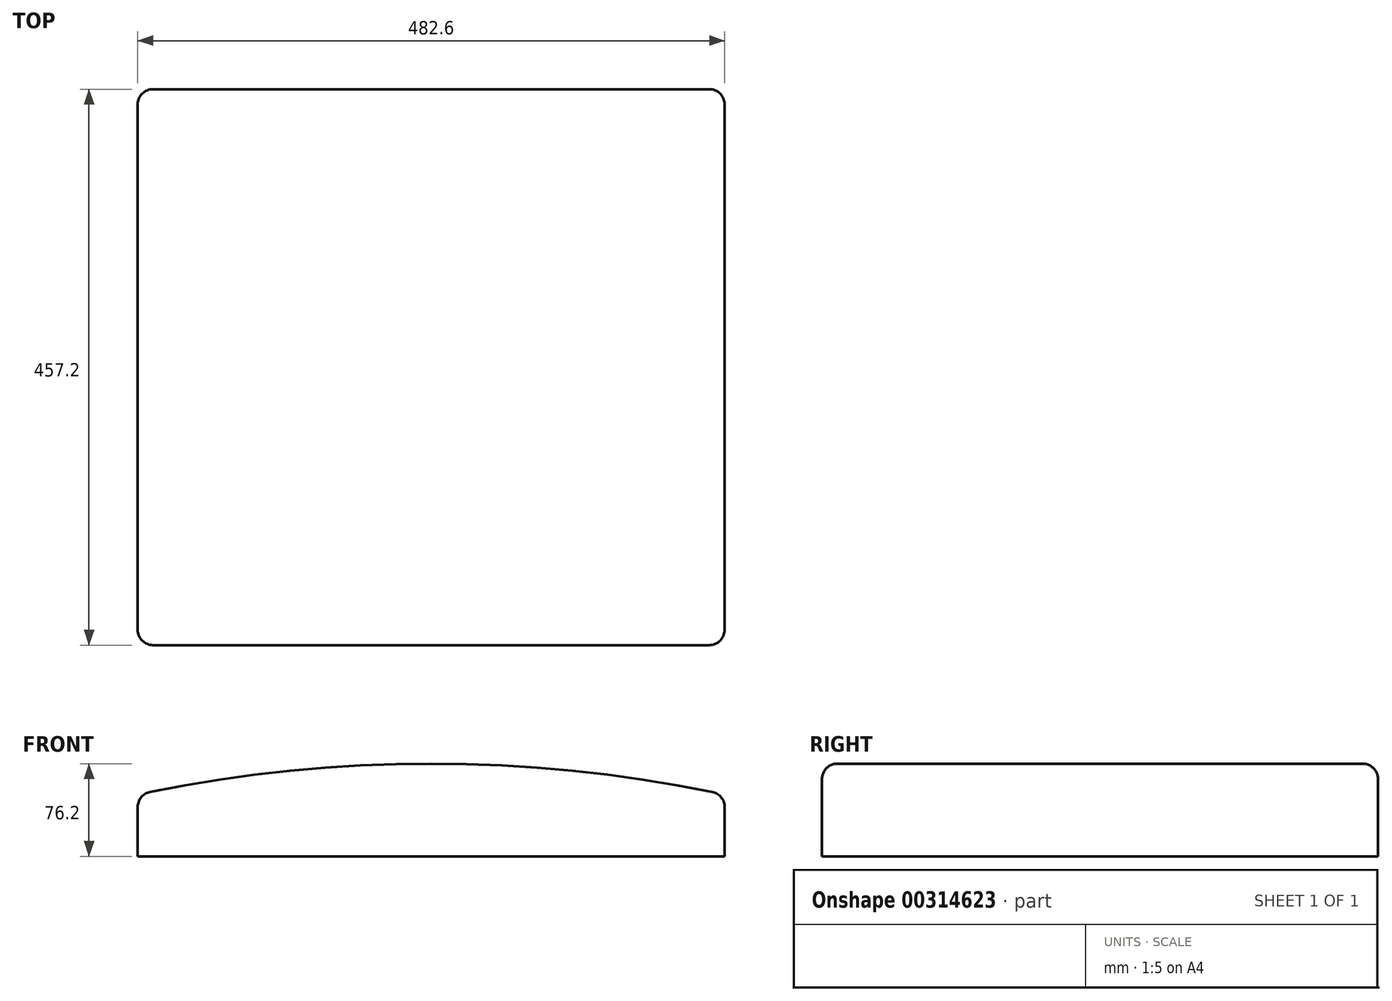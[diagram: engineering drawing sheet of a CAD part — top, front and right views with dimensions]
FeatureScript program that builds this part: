
annotation { "Feature Type Name" : "Feature", "Feature Type Description" : "" }
export const myFeature = defineFeature(function(context is Context, id is Id, definition is map)
    precondition{}
    {
        {
            var Q0;
            Q0=qCreatedBy(makeId("Front.planeOp"),FACE);
            var sketch = newSketch(context, id + "F0", { "sketchPlane" : qUnion([Q0])});
            skLineSegment(sketch, "E0.bottom", {"start": v(241.3, -25.4) * mm, "end": v(-241.3, -25.4) * mm});
            skLineSegment(sketch, "E0.top", {"start": v(241.3, 25.4) * mm, "end": v(-241.3, 25.4) * mm});
            skLineSegment(sketch, "E0.left", {"start": v(241.3, -25.4) * mm, "end": v(241.3, 25.4) * mm});
            skLineSegment(sketch, "E0.right", {"start": v(-241.3, -25.4) * mm, "end": v(-241.3, 25.4) * mm});
            skPoint(sketch, "E0.middle", {"position": v(0, 0) * mm});
            skArc(sketch, "E1", {"start": v(241.3, 25.4) * mm, "mid": v(0, 50.8) * mm, "end": v(-241.3, 25.4) * mm});
            skSolve(sketch);
        }
        {
            var Q0;
            Q0=makeQuery(id+"F0.imprint","IMPRINT",FACE,{"disambiguationData":[TD([[makeQuery(id+"F0.imprint","IMPRINT",EDGE,{"derivedFrom":sQuery(id+"F0.wireOp",EDGE,"E0.top")}),-1.0]])]});
            extrude(context, id + "F1", {"entities" : qUnion([Q0]), "endBound" : BoundingType.SYMMETRIC, "depth" : 457.2 * mm});
        }
        {
            var Q0;
            Q0 = qSketchRegion(id + "F0", true);
            extrude(context, id + "F2", {"entities" : qUnion([Q0]), "operationType" : NewBodyOperationType.ADD, "endBound" : BoundingType.SYMMETRIC, "depth" : 457.2 * mm});
        }
        {
            var Q0;
            Q0=makeQuery(id+"F2.opExtrude","CAP_EDGE",EDGE,{"disambiguationData":[OSD([sQuery(id+"F0.wireOp",EDGE,"E0.right")])],"isStart":true});
            var Q1;
            Q1=makeQuery(id+"F2.opExtrude","CAP_EDGE",EDGE,{"disambiguationData":[OSD([sQuery(id+"F0.wireOp",EDGE,"E0.right")])],"isStart":false});
            var Q2;
            Q2=makeQuery(id+"F2.opExtrude","CAP_EDGE",EDGE,{"disambiguationData":[OSD([sQuery(id+"F0.wireOp",EDGE,"E0.left")])],"isStart":true});
            var Q3;
            Q3=makeQuery(id+"F2.opExtrude","CAP_EDGE",EDGE,{"disambiguationData":[OSD([sQuery(id+"F0.wireOp",EDGE,"E0.left")])],"isStart":false});
            var Q4;
            {var subQ0=sQuery(id+"F0.wireOp",EDGE,"E1");var subQ1=sQuery(id+"F0.wireOp",EDGE,"E0.left");var subQ2=sQuery(id+"F0.wireOp",EDGE,"E0.top");Q4=makeQuery(id+"F2.boolean.opBoolean","MERGE",EDGE,{"derivedFrom":[makeQuery(id+"F1.opExtrude","SWEPT_EDGE",EDGE,{"disambiguationData":[OSD([subQ2,subQ1,subQ0])]}),makeQuery(id+"F2.opExtrude","SWEPT_EDGE",EDGE,{"disambiguationData":[OSD([subQ2,subQ1,subQ0])]})]});}
            var Q5;
            Q5=makeQuery(id+"F1.opExtrude","CAP_EDGE",EDGE,{"disambiguationData":[OSD([sQuery(id+"F0.wireOp",EDGE,"E1")])],"isStart":false});
            var Q6;
            Q6=makeQuery(id+"F1.opExtrude","CAP_EDGE",EDGE,{"disambiguationData":[OSD([sQuery(id+"F0.wireOp",EDGE,"E1")])],"isStart":true});
            var Q7;
            {var subQ0=sQuery(id+"F0.wireOp",EDGE,"E1");var subQ1=sQuery(id+"F0.wireOp",EDGE,"E0.right");var subQ2=sQuery(id+"F0.wireOp",EDGE,"E0.top");Q7=makeQuery(id+"F2.boolean.opBoolean","MERGE",EDGE,{"derivedFrom":[makeQuery(id+"F1.opExtrude","SWEPT_EDGE",EDGE,{"disambiguationData":[OSD([subQ2,subQ1,subQ0])]}),makeQuery(id+"F2.opExtrude","SWEPT_EDGE",EDGE,{"disambiguationData":[OSD([subQ2,subQ1,subQ0])]})]});}
            fillet(context, id + "F3", {"entities" : qUnion([Q0, Q1, Q2, Q3, Q4, Q5, Q6, Q7]), "radius" : 12.7 * mm, "tangentPropagation" : true, "allowEdgeOverflow" : false});
        }
    });
